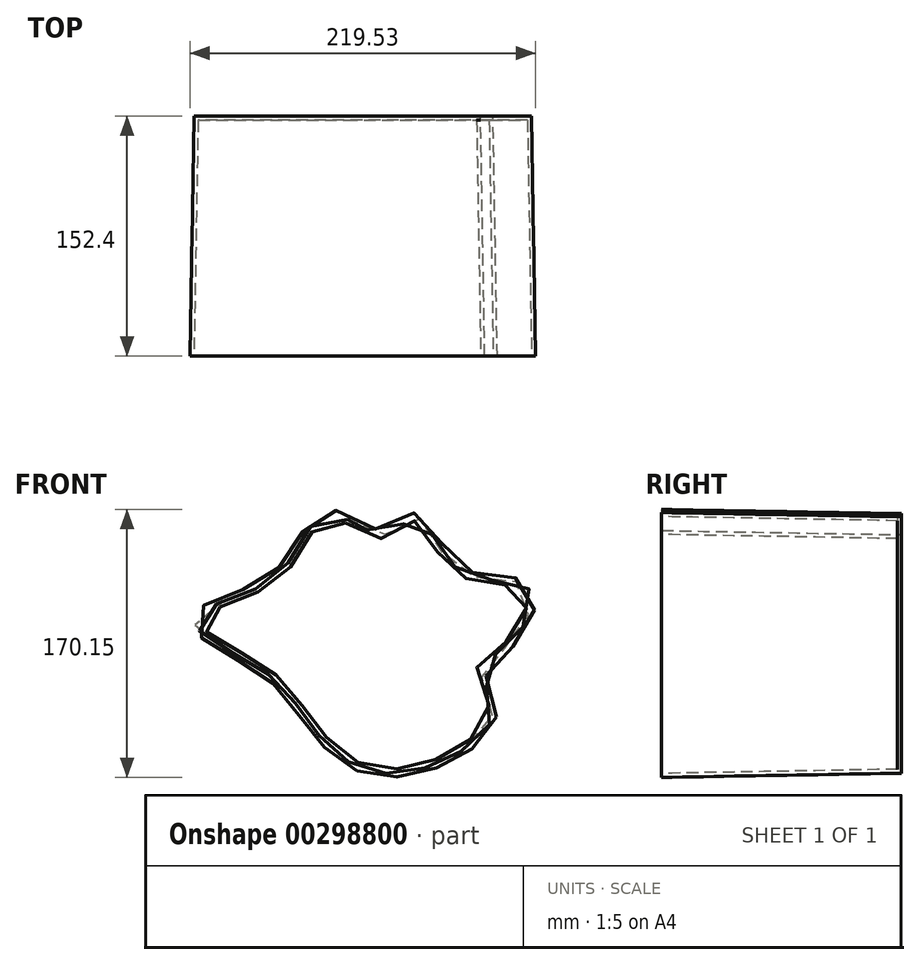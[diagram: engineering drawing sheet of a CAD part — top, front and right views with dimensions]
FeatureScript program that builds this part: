
annotation { "Feature Type Name" : "Feature", "Feature Type Description" : "" }
export const myFeature = defineFeature(function(context is Context, id is Id, definition is map)
    precondition{}
    {
        {
            var Q0;
            Q0=qCreatedBy(makeId("Front.planeOp"),FACE);
            var sketch = newSketch(context, id + "F0", { "sketchPlane" : qUnion([Q0])});
            skPoint(sketch, "E0.middle", {"position": v(0, 0) * mm});
            skPoint(sketch, "E1.visualSharp", {"position": v(-76.2, 50.8) * mm});
            skPoint(sketch, "E2.visualSharp", {"position": v(76.2, 50.8) * mm});
            skPoint(sketch, "E3.visualSharp", {"position": v(76.2, -50.8) * mm});
            skPoint(sketch, "E4.visualSharp", {"position": v(-76.2, -50.8) * mm});
            skPoint(sketch, "E5.9.internal.snap0", {"position": v(0, -50.8) * mm});
            skFitSpline(sketch, "E5", {"points": [v(-50.8, 50.8) * mm, v(-31.06, 72.23) * mm, v(4.29, 59.02) * mm, v(24.4, 70.22) * mm, v(52.27, 35.45) * mm, v(94.8, 25.4) * mm, v(84.74, -9.09) * mm, v(64.92, -26.04) * mm, v(72.39, -56.21) * mm, v(0, -92.14) * mm, v(-50.8, -50.8) * mm, v(-76.2, -25.4) * mm, v(-117.03, 4.24) * mm, v(-76.2, 25.4) * mm, v(-50.8, 50.8) * mm]});
            skPoint(sketch, "E6.orphan", {"position": v(50.8, -50.8) * mm});
            skPoint(sketch, "E2.filletArc.start.orphan", {"position": v(76.2, 25.4) * mm});
            skSolve(sketch);
        }
        {
            var Q0;
            Q0=makeQuery(id+"F0.imprint","IMPRINT",FACE,{"disambiguationData":[TD([[makeQuery(id+"F0.imprint","IMPRINT",EDGE,{"derivedFrom":sQuery(id+"F0.wireOp",EDGE,"E5")}),-1.0]])]});
            extrude(context, id + "F1", {"entities" : qUnion([Q0]), "depth" : 152.4 * mm, "hasDraft" : true, "draftAngle" : 1 * degree});
        }
        {
            var Q0;
            Q0=makeQuery(id+"F1.opExtrude","CAP_FACE",FACE,{"disambiguationData":[OSD([sQuery(id+"F0.wireOp",EDGE,"E5")])],"isStart":false});
            shell(context, id + "F2", {"entities" : qUnion([Q0]), "thickness" : 2.54 * mm});
        }
    });
